# Revit family: Faucet_Touchless-Lavatory-KOHLER-Oblo_Tall-K-103B86_1
name_source: partatom
category: Plumbing Fixtures
revit_build: Autodesk Revit 2017 (Build: 20160225_1515(x64)
units: mm (PartAtom-declared; Revit-internal decimal feet)

## family parameters
Cut with Voids When Loaded = No
Host = Face
OmniClass Number = 23.31.11.00
Part Type = Normal
Room Calculation Point = No
Round Connector Dimension = Use Diameter
Shared = No

## types (1)
- CP-Polished Chrome
    ADA Compliant = Yes
    Apparent Load = 1800 VA
    Assembly Code = D2010
    CW Connection = No
    Cold Water Inlet = Cold Water Inlet
    Date Modified = 01/08/2020
    Default Elevation = 36"
    Description = Touchless faucet with Kinesis sensor technology, AC-powered
    Drain Included = Yes
    Electrical Connector = Yes
    Electrical Note = One dedicated circuit required, protected with Class A Ground-Fault Circuit-Interrupter (GFCI). Outside North America, this device may be known as a Residual Current Device (RCD)
    Finish = Kohler-Metal-CP-Polished_Chrome
    Flow Rate = 1 GPM
    HW Connection = Yes
    Height = 13 7/8"
    Hot Water Inlet = Hot Water Inlet
    Length = 5 3/16"
    Manufacturer = KOHLER Co.
    MasterFormat 1995 = 15410
    MasterFormat 2004 = 22.41.39
    Material = Brass Construction
    Model = K-103B86-SANA-CP
    Pressure = 60.00 psi
    Product Documentation Link = https://www.us.kohler.com
    Product Name = Oblo Tall
    Product Page URL = http://www.us.kohler.com
    Spout Reach = 5 3/16"
    Tempered Water Inlet = Tempered Water Inlet
    URL = https://www.us.kohler.com
    Vent Connection = No
    Voltage = 120 V
    Waste Connection = No
    Waste Water Outlet = Waste Water Outlet
    WaterSense Certified = No
    Width = 2 5/16"

## geometry (parser evidence)
native form markers: Sweep x5
no freeform markers — native parametric forms only
